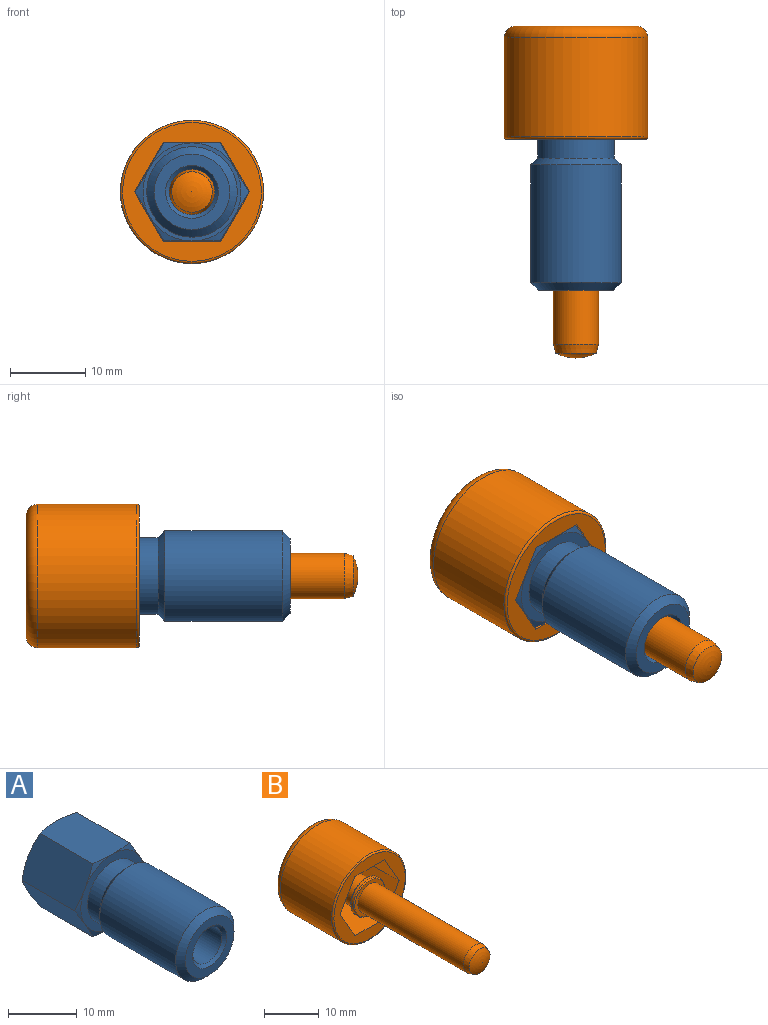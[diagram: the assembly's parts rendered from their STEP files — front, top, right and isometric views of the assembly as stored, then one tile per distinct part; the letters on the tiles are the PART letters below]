
ASSEMBLY  parts=2 mates=1
PART A: 40 faces, bbox 15.6x32.6x15.6 mm
  f0: cone r=6.5mm half-angle=75deg, axis (0,1,0), area 3.7mm2, adj f12,f35,f36
  f1: cone r=6.5mm half-angle=75deg, axis (0,1,0), area 3.7mm2, adj f12,f36,f37
  f2: cone r=6.5mm half-angle=75deg, axis (0,1,0), area 3.7mm2, adj f12,f34,f35
  f3: cone r=6.5mm half-angle=75deg, axis (0,1,0), area 3.7mm2, adj f12,f37,f38
  f4: cone r=6.5mm half-angle=75deg, axis (0,1,0), area 3.7mm2, adj f12,f34,f39
  f5: cylinder r=3mm len=19.5mm, axis (0,-1,0), area 367.6mm2, adj f6,f33
  f6: cone r=3mm half-angle=45deg, axis (0,-1,0), area 14.4mm2, adj f5,f7
  f7: plane 10x10mm, normal (0,-1,0), area 40.1mm2, adj f6,f8
  f8: cone r=5mm half-angle=45deg, axis (0,1,0), area 48.9mm2, adj f7,f9
  f9: cylinder r=6mm len=15.6mm, axis (0,-1,0), area 588.1mm2, adj f8,f10
  f10: cone r=6mm half-angle=45deg, axis (0,-1,0), area 44.4mm2, adj f9,f11
  f11: cylinder r=5.1mm len=10.2mm, axis (0,-1,0), area 80.1mm2, adj f10,f12
  f12: plane 13x13mm, normal (0,-1,0), area 51mm2, adj f0,f1,f2,f3,f4,f11,f13
  f13: cone r=6.5mm half-angle=75deg, axis (0,1,0), area 3.7mm2, adj f12,f38,f39
  f14: cone r=8.33mm half-angle=60deg, axis (0,-1,0), area 43.3mm2, adj f15,f34,f35,f36,f37,f38,f39
  f15: plane 11.84x11.84mm, normal (0,1,0), area 81.9mm2, adj f14,f16
  f16: cylinder r=3mm len=6mm, axis (0,-1,0), area 28.3mm2, adj f15,f17
  f17: plane 7.6x7.6mm, normal (0,-1,0), area 17.1mm2, adj f16,f18
  f18: torus R=3.8mm, axis (0,-1,0), area 7.8mm2, adj f17,f19
  f19: cylinder r=4mm len=8mm, axis (0,-1,0), area 15.1mm2, adj f18,f20
  f20: torus R=3.8mm, axis (0,-1,0), area 7.8mm2, adj f19,f21
  f21: plane 7.6x7.6mm, normal (0,1,0), area 17.1mm2, adj f20,f22
  f22: cylinder r=3mm len=6mm, axis (0,-1,0), area 103.7mm2, adj f21,f23
  f23: plane 7.6x7.6mm, normal (0,-1,0), area 17.1mm2, adj f22,f24
  f24: torus R=3.8mm, axis (0,-1,0), area 7.8mm2, adj f23,f25
  f25: cylinder r=4mm len=8mm, axis (0,-1,0), area 15.1mm2, adj f24,f26
  f26: torus R=3.8mm, axis (0,-1,0), area 7.8mm2, adj f25,f27
  f27: plane 7.6x7.6mm, normal (0,1,0), area 17.1mm2, adj f26,f28
  f28: cylinder r=3mm len=6mm, axis (0,-1,0), area 37.7mm2, adj f27,f29
  f29: plane 7.6x7.6mm, normal (0,-1,0), area 17.1mm2, adj f28,f30
  f30: torus R=3.8mm, axis (0,-1,0), area 7.8mm2, adj f29,f31
  f31: cylinder r=4mm len=8mm, axis (0,-1,0), area 15.1mm2, adj f30,f32
  f32: torus R=3.8mm, axis (0,-1,0), area 7.8mm2, adj f31,f33
  f33: plane 7.6x7.6mm, normal (0,1,0), area 17.1mm2, adj f5,f32
  f34: plane 12.23x7.06mm, normal (-0.87,0,-0.5), area 85.4mm2, adj f2,f4,f14,f35,f39
  f35: plane 12.29x8.13mm, normal (0,0,-1), area 85.4mm2, adj f0,f2,f14,f34,f36
  f36: plane 12.23x7.06mm, normal (0.87,0,-0.5), area 85.4mm2, adj f0,f1,f14,f35,f37
  f37: plane 12.23x7.06mm, normal (0.87,0,0.5), area 85.4mm2, adj f1,f3,f14,f36,f38
  f38: plane 12.23x8.07mm, normal (0,0,1), area 85.4mm2, adj f3,f13,f14,f37,f39
  f39: plane 12.23x7.06mm, normal (-0.87,0,0.5), area 85.4mm2, adj f4,f13,f14,f34,f38
PART B: 22 faces, bbox 20.6x44x20.6 mm
  f0: plane 15.24x13.2mm, normal (0,-1,0), area 122.6mm2, adj f1,f10,f11,f12,f13,f14,f15
  f1: cylinder r=3mm len=11mm, axis (0,-1,0), area 207.3mm2, adj f0,f2
  f2: plane 7.6x7.6mm, normal (0,1,0), area 17.1mm2, adj f1,f3
  f3: torus R=3.8mm, axis (0,-1,0), area 7.8mm2, adj f2,f4
  f4: cylinder r=4mm len=8mm, axis (0,-1,0), area 15.1mm2, adj f3,f5
  f5: torus R=3.8mm, axis (0,-1,0), area 7.8mm2, adj f4,f6
  f6: plane 7.6x7.6mm, normal (0,-1,0), area 17.1mm2, adj f5,f7
  f7: cylinder r=3mm len=27.2mm, axis (0,-1,0), area 512.6mm2, adj f6,f8
  f8: cone r=3mm half-angle=15deg, axis (0,1,0), area 21.6mm2, adj f7,f9
  f9: torus R=0mm, axis (0,-1,0), area 23.9mm2, adj f8
  f10: plane 12x6.6mm, normal (0.87,0,-0.5), area 91.5mm2, adj f0,f11,f15,f21
  f11: plane 12x6.6mm, normal (0.87,0,0.5), area 91.5mm2, adj f0,f10,f12,f21
  f12: plane 12x7.62mm, normal (0,0,1), area 91.5mm2, adj f0,f11,f13,f21
  f13: plane 12x6.6mm, normal (-0.87,0,0.5), area 91.5mm2, adj f0,f12,f14,f21
  f14: plane 12x6.6mm, normal (-0.87,0,-0.5), area 91.5mm2, adj f0,f13,f15,f21
  f15: plane 12x7.62mm, normal (0,0,-1), area 91.5mm2, adj f0,f10,f14,f21
  f16: torus R=0mm, axis (0,-1,0), area 155.7mm2, adj f17
  f17: plane 16x16mm, normal (0,1,0), area 45.9mm2, adj f16,f18
  f18: torus R=8mm, axis (0,-1,0), area 132.6mm2, adj f17,f19
  f19: cylinder r=9.5mm len=19mm, axis (0,-1,0), area 787.9mm2, adj f18,f20
  f20: torus R=9.2mm, axis (0,-1,0), area 27.8mm2, adj f19,f21
  f21: plane 18.4x18.4mm, normal (0,-1,0), area 115mm2, adj f10,f11,f12,f13,f14,f15,f20
PLACE A t=(-11.49,3.04,3.64)mm
PLACE B t=(-11.49,0.04,3.64)mm
MATE fastened A.f0 <-> B.f1  axis (0,-1,0) through (-11.49,3.04,3.64)mm
